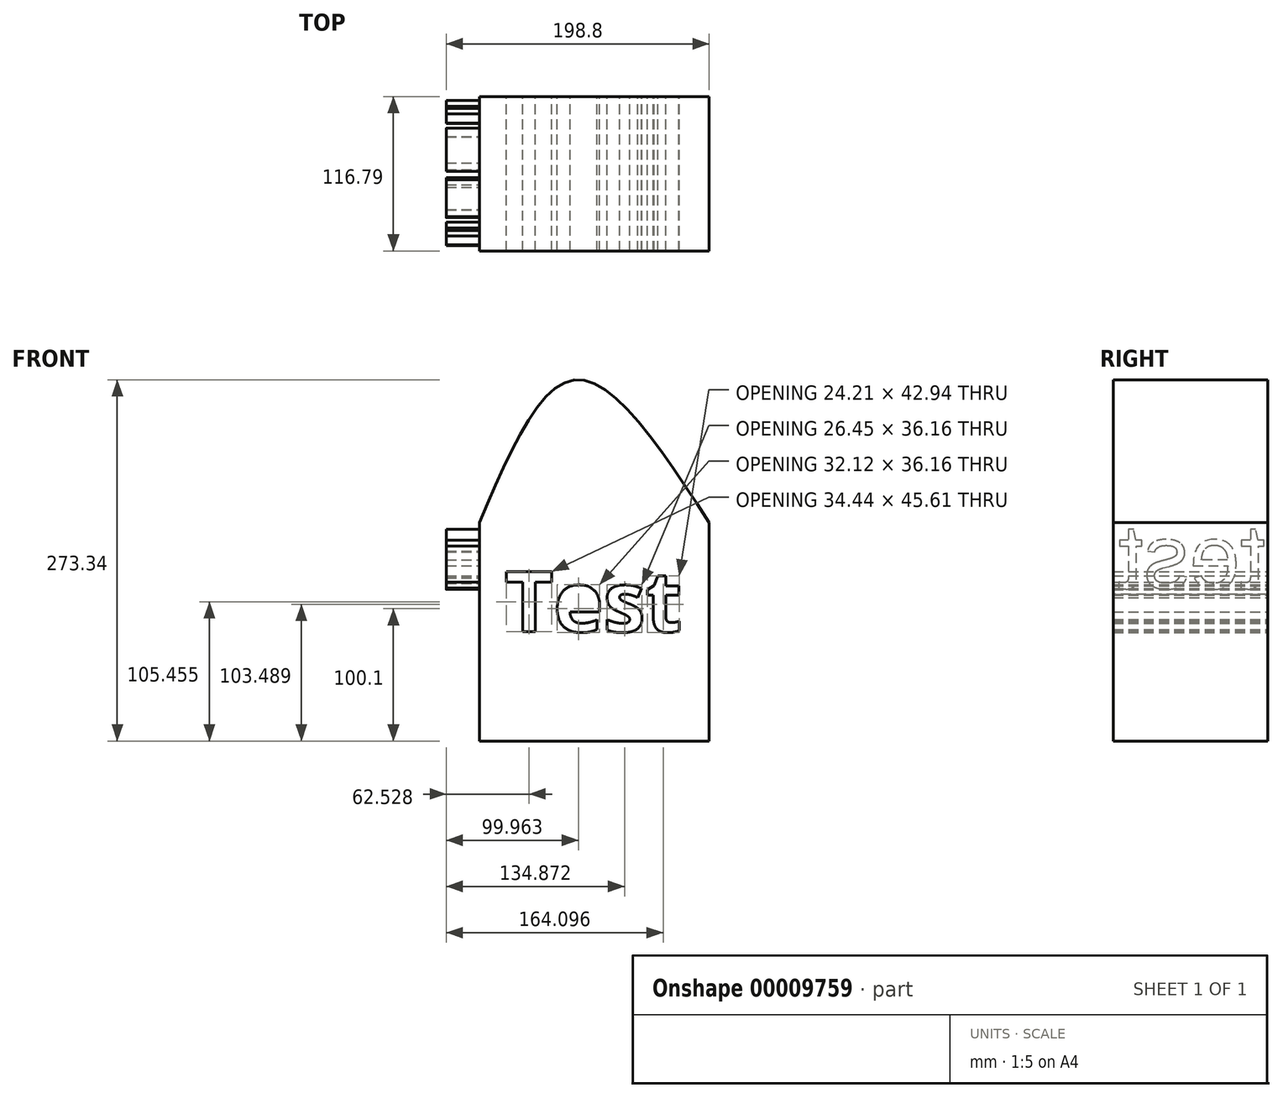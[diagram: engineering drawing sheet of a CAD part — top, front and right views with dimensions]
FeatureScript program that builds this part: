
annotation { "Feature Type Name" : "Feature", "Feature Type Description" : "" }
export const myFeature = defineFeature(function(context is Context, id is Id, definition is map)
    precondition{}
    {
        {
            var Q0;
            Q0=qCreatedBy(makeId("Front.planeOp"),FACE);
            var sketch = newSketch(context, id + "F0", { "sketchPlane" : qUnion([Q0])});
            skLineSegment(sketch, "E0.rect.bottom", {"start": v(86.9, 82.65) * mm, "end": v(-86.9, 82.65) * mm});
            skLineSegment(sketch, "E0.rect.top", {"start": v(86.9, -82.65) * mm, "end": v(-86.9, -82.65) * mm});
            skLineSegment(sketch, "E0.rect.left", {"start": v(86.9, 82.65) * mm, "end": v(86.9, -82.65) * mm});
            skLineSegment(sketch, "E0.rect.right", {"start": v(-86.9, 82.65) * mm, "end": v(-86.9, -82.65) * mm});
            skPoint(sketch, "E0.rect.middle", {"position": v(0, 0) * mm});
            skFitSpline(sketch, "E1", {"points": [v(-86.9, 82.65) * mm, v(-14.15, 190.62) * mm, v(86.9, 82.65) * mm], "startDerivative": vector(139.24, 327.66) * mm, "endDerivative": vector(207.62, -320.78) * mm});
            skText(sketch, "E2", { "text": "Test", "fontName": "OpenSans-Bold.ttf"});
            const initialGuessF0  = {"E2": [-0.06787, 0, 1, 0, 0.046]};
            skSetInitialGuess(sketch, initialGuessF0);
            skSolve(sketch);
        }
        {
            var Q0;
            Q0=makeQuery(id+"F0.imprint","IMPRINT",FACE,{"disambiguationData":[TD([[makeQuery(id+"F0.imprint","IMPRINT",EDGE,{"derivedFrom":sQuery(id+"F0.wireOp",EDGE,"E0.rect.bottom")}),1.0]])]});
            var Q1;
            Q1=makeQuery(id+"F0.imprint","IMPRINT",FACE,{"disambiguationData":[TD([[makeQuery(id+"F0.imprint","IMPRINT",EDGE,{"derivedFrom":sQuery(id+"F0.wireOp",EDGE,"E0.rect.bottom")}),-1.0]])]});
            extrude(context, id + "F1", {"entities" : qUnion([Q0, Q1]), "depth" : 116.8 * mm});
        }
        {
            var Q0;
            Q0=makeQuery(id+"F1.opExtrude","SWEPT_FACE",FACE,{"disambiguationData":[OSD([sQuery(id+"F0.wireOp",EDGE,"E0.rect.right")])]});
            var sketch = newSketch(context, id + "F2", { "sketchPlane" : qUnion([Q0])});
            skText(sketch, "E3", { "text": "test", "fontName": "Arimo-Regular.ttf"});
            const initialGuessF2  = {"E3": [0.0018, 0.03285, 1, 0, 0.0498]};
            skSetInitialGuess(sketch, initialGuessF2);
            skSolve(sketch);
        }
        {
            var Q0;
            Q0 = qSketchRegion(id + "F2", true);
            extrude(context, id + "F3", {"entities" : qUnion([Q0]), "operationType" : NewBodyOperationType.ADD, "depth" : 25 * mm});
        }
    });
